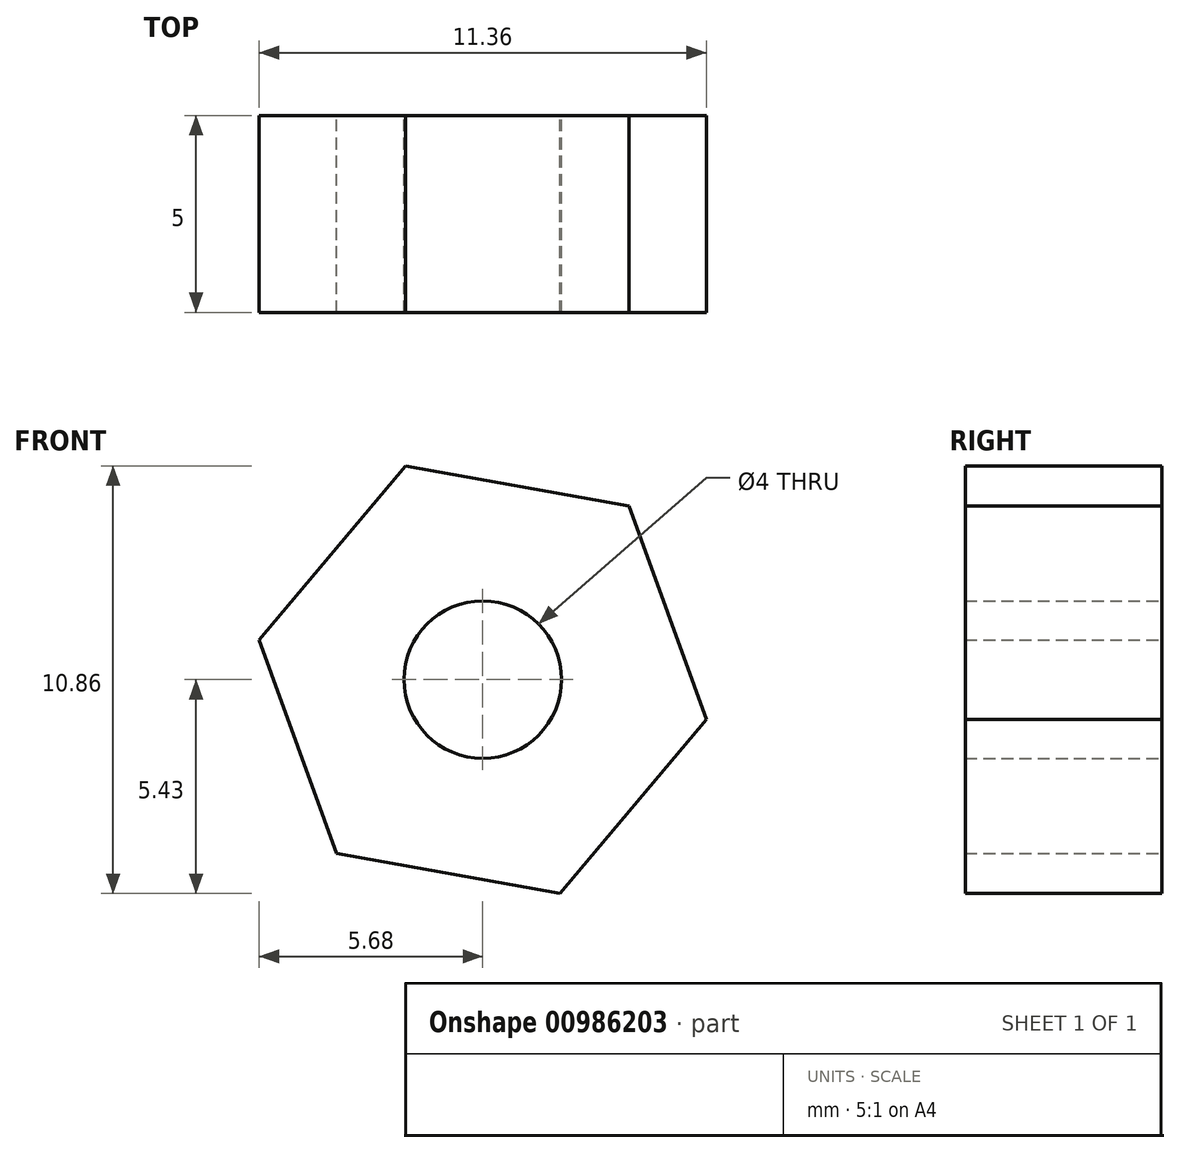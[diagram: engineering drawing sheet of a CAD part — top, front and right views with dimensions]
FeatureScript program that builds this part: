
annotation { "Feature Type Name" : "Feature", "Feature Type Description" : "" }
export const myFeature = defineFeature(function(context is Context, id is Id, definition is map)
    precondition{}
    {
        {
            var Q0;
            Q0=qCreatedBy(makeId("Front.planeOp"),FACE);
            var sketch = newSketch(context, id + "F0", { "sketchPlane" : qUnion([Q0])});
            skCircle(sketch, "E0.cCircle", {"center": v(0, 0) * mm, "radius": 5 * mm, "construction": true});
            skLineSegment(sketch, "E0.0", {"start": v(3.72, 4.42) * mm, "end": v(5.68, -1.01) * mm});
            skLineSegment(sketch, "E0.1", {"start": v(5.68, -1.01) * mm, "end": v(1.96, -5.43) * mm});
            skLineSegment(sketch, "E0.2", {"start": v(1.96, -5.43) * mm, "end": v(-3.72, -4.42) * mm});
            skLineSegment(sketch, "E0.3", {"start": v(-3.72, -4.42) * mm, "end": v(-5.68, 1.01) * mm});
            skLineSegment(sketch, "E0.4", {"start": v(-5.68, 1.01) * mm, "end": v(-1.96, 5.43) * mm});
            skLineSegment(sketch, "E0.5", {"start": v(-1.96, 5.43) * mm, "end": v(3.72, 4.42) * mm});
            skPoint(sketch, "E0.0.midPoint", {"position": v(4.7, 1.7) * mm});
            skCircle(sketch, "E1", {"center": v(0, 0) * mm, "radius": 2 * mm});
            skSolve(sketch);
        }
        {
            var Q0;
            Q0=makeQuery(id+"F0.imprint","IMPRINT",FACE,{"disambiguationData":[TD([[makeQuery(id+"F0.imprint","IMPRINT",EDGE,{"derivedFrom":sQuery(id+"F0.wireOp",EDGE,"E0.0")}),-1.0]])]});
            extrude(context, id + "F1", {"entities" : qUnion([Q0]), "depth" : 5 * mm, "offsetDistance" : 25 * mm});
        }
    });
